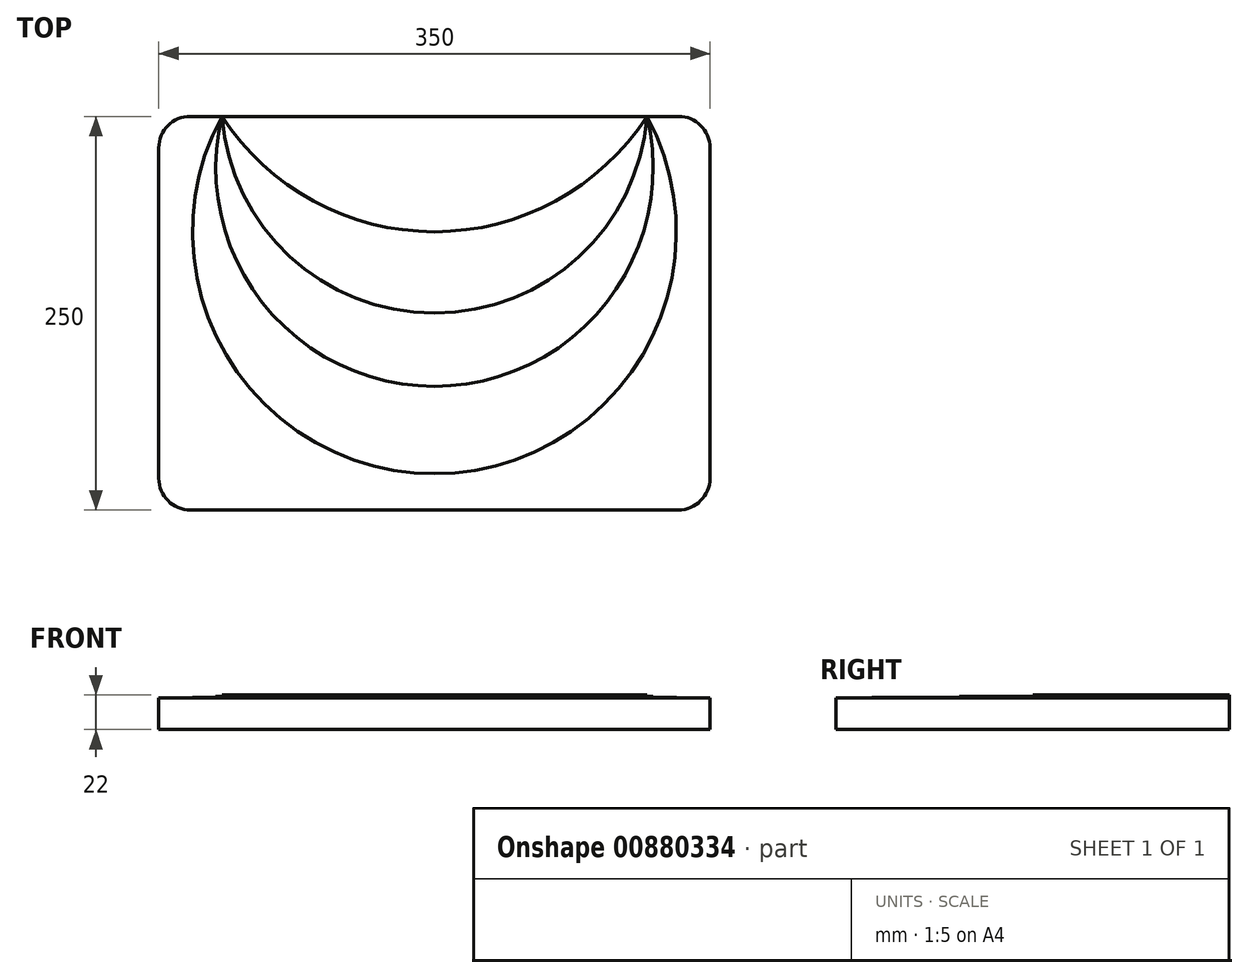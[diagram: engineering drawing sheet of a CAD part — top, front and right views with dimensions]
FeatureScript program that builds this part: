
annotation { "Feature Type Name" : "Feature", "Feature Type Description" : "" }
export const myFeature = defineFeature(function(context is Context, id is Id, definition is map)
    precondition{}
    {
        {
            var Q0;
            Q0=qCreatedBy(makeId("Top.planeOp"),FACE);
            var sketch = newSketch(context, id + "F0", { "sketchPlane" : qUnion([Q0])});
            skLineSegment(sketch, "E0.bottom", {"start": v(155, -125) * mm, "end": v(-155, -125) * mm});
            skLineSegment(sketch, "E0.top", {"start": v(155, 125) * mm, "end": v(-155, 125) * mm});
            skLineSegment(sketch, "E0.left", {"start": v(175, -105) * mm, "end": v(175, 105) * mm});
            skLineSegment(sketch, "E0.right", {"start": v(-175, -105) * mm, "end": v(-175, 105) * mm});
            skPoint(sketch, "E0.middle", {"position": v(0, 0) * mm});
            skArc(sketch, "E1", {"start": v(-135, 125) * mm, "mid": v(0, -101.98) * mm, "end": v(135, 125) * mm});
            skArc(sketch, "E2", {"start": v(-135, 125) * mm, "mid": v(0, -46.45) * mm, "end": v(135, 125) * mm});
            skArc(sketch, "E3", {"start": v(-135, 125) * mm, "mid": v(0, 0) * mm, "end": v(135, 125) * mm});
            skArc(sketch, "E4", {"start": v(-135, 125) * mm, "mid": v(0, 51.65) * mm, "end": v(135, 125) * mm});
            skPoint(sketch, "E5.visualSharp", {"position": v(-175, 125) * mm});
            skArc(sketch, "E5.filletArc", {"start": v(-155, 125) * mm, "mid": v(-169.14, 119.14) * mm, "end": v(-175, 105) * mm});
            skPoint(sketch, "E6.visualSharp", {"position": v(175, 125) * mm});
            skArc(sketch, "E6.filletArc", {"start": v(175, 105) * mm, "mid": v(169.14, 119.14) * mm, "end": v(155, 125) * mm});
            skPoint(sketch, "E7.visualSharp", {"position": v(175, -125) * mm});
            skArc(sketch, "E7.filletArc", {"start": v(155, -125) * mm, "mid": v(169.14, -119.14) * mm, "end": v(175, -105) * mm});
            skPoint(sketch, "E8.visualSharp", {"position": v(-175, -125) * mm});
            skArc(sketch, "E8.filletArc", {"start": v(-175, -105) * mm, "mid": v(-169.14, -119.14) * mm, "end": v(-155, -125) * mm});
            skSolve(sketch);
        }
        {
            var Q0;
            Q0=makeQuery(id+"F0.imprint","IMPRINT",FACE,{"disambiguationData":[TD([[makeQuery(id+"F0.imprint","IMPRINT",EDGE,{"derivedFrom":sQuery(id+"F0.wireOp",EDGE,"E0.bottom")}),-1.0]])]});
            var Q1;
            Q1=makeQuery(id+"F0.imprint","IMPRINT",FACE,{"disambiguationData":[TD([[makeQuery(id+"F0.imprint","IMPRINT",EDGE,{"derivedFrom":sQuery(id+"F0.wireOp",EDGE,"E1")}),1.0]])]});
            var Q2;
            Q2=makeQuery(id+"F0.imprint","IMPRINT",FACE,{"disambiguationData":[TD([[makeQuery(id+"F0.imprint","IMPRINT",EDGE,{"derivedFrom":sQuery(id+"F0.wireOp",EDGE,"E2")}),1.0]])]});
            var Q3;
            Q3=makeQuery(id+"F0.imprint","IMPRINT",FACE,{"disambiguationData":[TD([[makeQuery(id+"F0.imprint","IMPRINT",EDGE,{"derivedFrom":sQuery(id+"F0.wireOp",EDGE,"E3")}),1.0]])]});
            var Q4;
            {var subQ0=sQuery(id+"F0.wireOp",EDGE,"E4");Q4=makeQuery(id+"F0.imprint","IMPRINT",FACE,{"disambiguationData":[TD([[makeQuery(id+"F0.imprint","IMPRINT",EDGE,{"derivedFrom":subQ0}),1.0]])]});}
            extrude(context, id + "F1", {"entities" : qUnion([Q0, Q1, Q2, Q3, Q4]), "depth" : 20 * mm, "offsetDistance" : 25 * mm});
        }
        {
            var Q0;
            Q0=makeQuery(id+"F1.opExtrude","CAP_FACE",FACE,{"disambiguationData":[OSD([sQuery(id+"F0.wireOp",EDGE,"E0.bottom"),sQuery(id+"F0.wireOp",EDGE,"E0.top"),sQuery(id+"F0.wireOp",EDGE,"E0.left"),sQuery(id+"F0.wireOp",EDGE,"E0.right"),sQuery(id+"F0.wireOp",EDGE,"E5.filletArc"),sQuery(id+"F0.wireOp",EDGE,"E6.filletArc"),sQuery(id+"F0.wireOp",EDGE,"E7.filletArc"),sQuery(id+"F0.wireOp",EDGE,"E8.filletArc")])],"isStart":false});
            var sketch = newSketch(context, id + "F2", { "sketchPlane" : qUnion([Q0])});
            skArc(sketch, "E9.0", {"start": v(-135, 125) * mm, "mid": v(0, -101.98) * mm, "end": v(135, 125) * mm});
            skArc(sketch, "E10.0", {"start": v(-135, 125) * mm, "mid": v(0, -46.45) * mm, "end": v(135, 125) * mm});
            skArc(sketch, "E11.0", {"start": v(-135, 125) * mm, "mid": v(0, 0) * mm, "end": v(135, 125) * mm});
            skArc(sketch, "E12.0", {"start": v(-135, 125) * mm, "mid": v(0, 51.65) * mm, "end": v(135, 125) * mm});
            skSolve(sketch);
        }
        {
            var Q0;
            {var subQ0=sQuery(id+"F2.wireOp",EDGE,"E12.0");Q0=makeQuery(id+"F2.imprint","IMPRINT",FACE,{"disambiguationData":[TD([[makeQuery(id+"F2.imprint","IMPRINT",EDGE,{"derivedFrom":subQ0}),1.0]])]});}
            extrude(context, id + "F3", {"entities" : qUnion([Q0]), "operationType" : NewBodyOperationType.ADD, "depth" : 1 * mm, "offsetDistance" : 25 * mm});
        }
        {
            var Q0;
            Q0=makeQuery(id+"F2.imprint","IMPRINT",FACE,{"disambiguationData":[TD([[makeQuery(id+"F2.imprint","IMPRINT",EDGE,{"derivedFrom":sQuery(id+"F2.wireOp",EDGE,"E11.0")}),1.0]])]});
            extrude(context, id + "F4", {"entities" : qUnion([Q0]), "operationType" : NewBodyOperationType.ADD, "depth" : 2 * mm, "offsetDistance" : 25 * mm});
        }
        {
            var Q0;
            Q0=makeQuery(id+"F2.imprint","IMPRINT",FACE,{"disambiguationData":[TD([[makeQuery(id+"F2.imprint","IMPRINT",EDGE,{"derivedFrom":sQuery(id+"F2.wireOp",EDGE,"E10.0")}),1.0]])]});
            extrude(context, id + "F5", {"entities" : qUnion([Q0]), "operationType" : NewBodyOperationType.ADD, "depth" : 1 * mm, "offsetDistance" : 25 * mm});
        }
        {
            var Q0;
            Q0=makeQuery(id+"F2.imprint","IMPRINT",FACE,{"disambiguationData":[TD([[makeQuery(id+"F2.imprint","IMPRINT",EDGE,{"derivedFrom":sQuery(id+"F2.wireOp",EDGE,"E9.0")}),1.0]])]});
            extrude(context, id + "F6", {"entities" : qUnion([Q0]), "operationType" : NewBodyOperationType.ADD, "depth" : 0.5 * mm, "offsetDistance" : 25 * mm});
        }
    });
